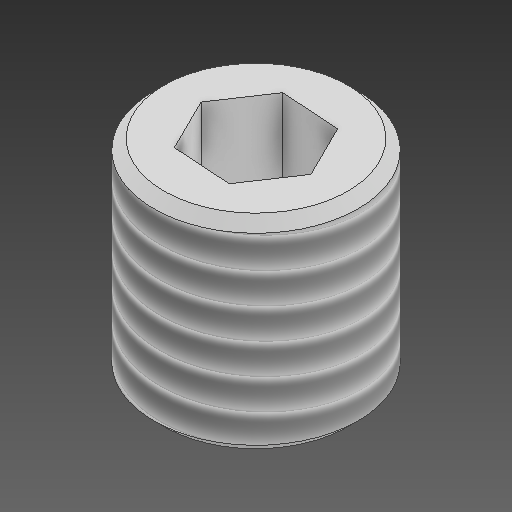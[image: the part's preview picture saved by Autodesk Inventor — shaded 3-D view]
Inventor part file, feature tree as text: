
AUTODESK INVENTOR PART (.ipt)
format: ipt  version: 2021 (Build 250183000, 183)  size: 179,200 bytes
history: native  units: in
note: dims shown in document units (in); Inventor stores cm internally (conversion verified against a paired STEP export)
features: other x3, sketch x2
ambient origin geometry x8: Origin, YZ Plane, XZ Plane, XY Plane, X Axis, Y Axis, Z Axis, Center Point
bodies: Solid1 (feature_tree)
feature tree (5):
  other  "M10_HEX.ipt"
  other  "Solid1::M10_HEX.ipt"
  other  "TaggingFeature1"
  sketch  "Sketch1"  dims[d0=0.3937in]
  sketch  "Sketch2"
